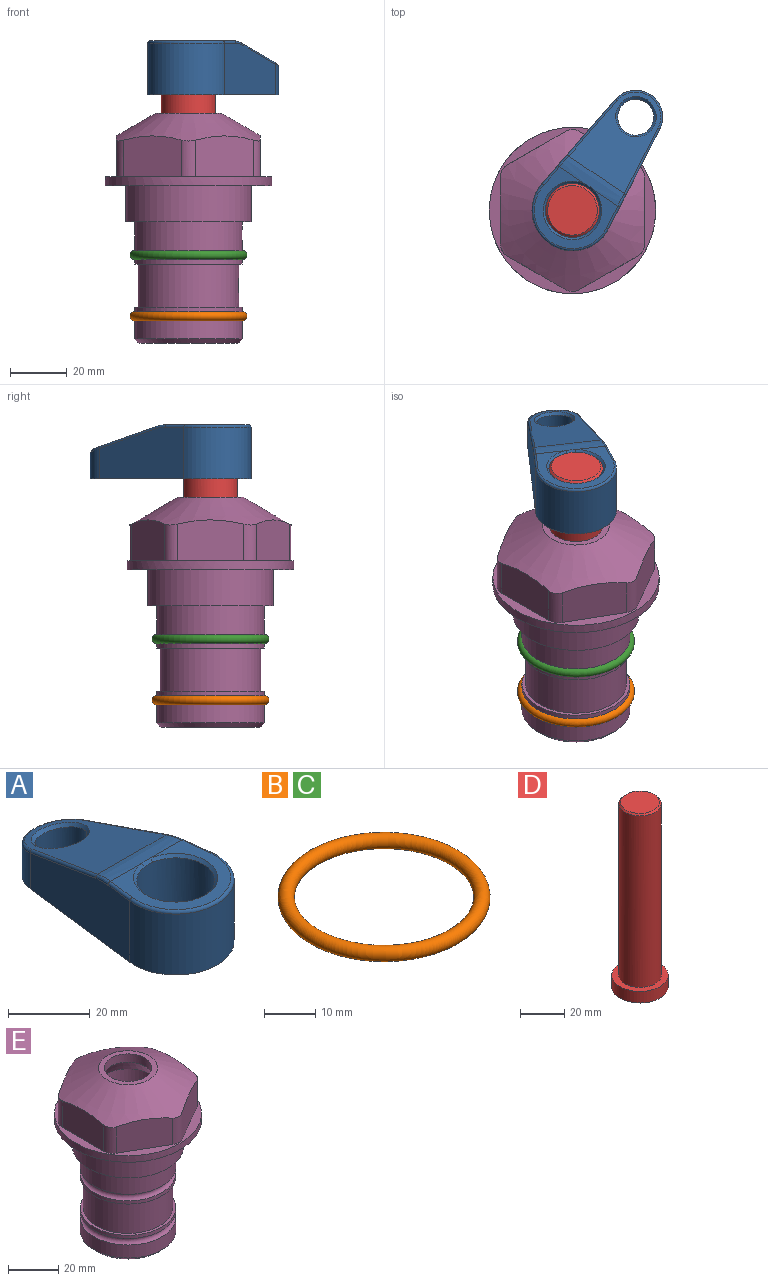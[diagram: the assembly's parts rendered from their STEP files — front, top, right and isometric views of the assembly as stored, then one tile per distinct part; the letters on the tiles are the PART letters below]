
ASSEMBLY  parts=5 mates=4
PART A: 31 faces, bbox 31.7x65.5x19.8 mm
  f0: plane 39.12x18.26mm, normal (0.99,0.12,0), area 612.2mm2, adj f1,f4,f7,f11,f13,f15
  f1: cylinder r=9.53mm len=18.91mm, axis (0,0,-1), area 296.1mm2, adj f0,f2,f7,f17
  f2: plane 39.12x18.26mm, normal (-0.99,0.12,0), area 612.2mm2, adj f1,f4,f7,f12,f14,f16
  f3: cylinder r=6.35mm len=12.7mm, axis (0,0,-1), area 362.4mm2, adj f7,f18
  f4: cylinder r=14.29mm len=28.58mm, axis (0,0,-1), area 882.2mm2, adj f0,f2,f7,f10
  f5: cylinder r=9.53mm len=19.05mm, axis (0,0,-1), area 1092.6mm2, adj f7,f19,f20
  f6: plane 26.99x23.69mm, normal (0,0,1), area 216.2mm2, adj f9,f10,f11,f12,f19
  f7: plane 63.5x28.58mm, normal (0,0,-1), area 661.8mm2, adj f0,f1,f2,f3,f4,f5,f22,f23
  f8: plane 33.52x23.6mm, normal (0,0.26,0.97), area 486mm2, adj f9,f15,f16,f17,f18
  f9: cylinder r=19.05mm len=24.72mm, axis (1,0,0), area 120.4mm2, adj f6,f8,f13,f14,f20
  f10: torus R=13.49mm, axis (0,0,1), area 59mm2, adj f4,f6,f11,f12
  f11: cylinder r=0.79mm len=8.67mm, axis (0.12,-0.99,0), area 10.8mm2, adj f0,f6,f10,f13
  f12: cylinder r=0.79mm len=8.67mm, axis (0.12,0.99,0), area 10.8mm2, adj f2,f6,f10,f14
  f13: bspline ~4.95x1.42mm, area 6.1mm2, adj f0,f9,f11,f15
  f14: bspline ~4.95x1.42mm, area 6.1mm2, adj f2,f9,f12,f16
  f15: cylinder r=0.79mm len=25.95mm, axis (0.12,-0.96,0.26), area 32.9mm2, adj f0,f8,f13,f17
  f16: cylinder r=0.79mm len=25.95mm, axis (0.12,0.96,-0.26), area 32.9mm2, adj f2,f8,f14,f17
  f17: bspline ~18.91x8.38mm, area 30mm2, adj f1,f8,f15,f16
  f18: bspline ~14.29x14.29mm, area 48.3mm2, adj f3,f8
  f19: cone r=9.53mm half-angle=45deg, axis (0,0,1), area 66.5mm2, adj f5,f6,f20
  f20: bspline ~3.22x0.96mm, area 3.5mm2, adj f5,f9,f19
  f21: plane 2.75x2.72mm, normal (0,0,-1), area 2.9mm2, adj f23,f25,f28
  f22: plane 23.05x15.88mm, normal (-0.99,-0.12,0), area 323.6mm2, adj f7,f25,f26,f27,f28,f29
  f23: plane 23.05x15.88mm, normal (0.99,-0.12,0), area 323.6mm2, adj f7,f21,f25,f27,f28,f30
  f24: cylinder r=9.53mm len=10.69mm, axis (0,0,-1), area 114.7mm2, adj f7,f27,f29,f30
  f25: cylinder r=12.7mm len=20.59mm, axis (0,0,-1), area 381.1mm2, adj f7,f21,f22,f23,f26,f28
  f26: plane 2.75x2.72mm, normal (0,0,-1), area 2.9mm2, adj f22,f25,f28
  f27: plane 19.72x18.37mm, normal (0,-0.26,-0.97), area 291.8mm2, adj f22,f23,f24,f28,f29,f30
  f28: cylinder r=15.88mm len=19.92mm, axis (1,0,0), area 54.8mm2, adj f21,f22,f23,f25,f26,f27
  f29: cylinder r=1.59mm len=11mm, axis (0,0,-1), area 34.7mm2, adj f7,f22,f24,f27
  f30: cylinder r=1.59mm len=11mm, axis (0,0,-1), area 34.7mm2, adj f7,f23,f24,f27
PART B: 1 faces, bbox 44.7x44.7x3.2 mm
  f0: torus R=19.05mm, axis (0,0,1), area 1193.9mm2
PART C: same geometry as B
PART D: 6 faces, bbox 25.4x25.4x101.6 mm
  f0: plane 17.46x17.46mm, normal (0,0,1), area 239.5mm2, adj f5
  f1: plane 25.4x25.4mm, normal (0,0,-1), area 506.7mm2, adj f2
  f2: cylinder r=12.7mm len=25.4mm, axis (0,0,1), area 506.7mm2, adj f1,f3
  f3: plane 25.4x25.4mm, normal (0,0,1), area 221.7mm2, adj f2,f4
  f4: cylinder r=9.53mm len=94.46mm, axis (0,0,1), area 5653mm2, adj f3,f5
  f5: cone r=8.73mm half-angle=45deg, axis (0,0,-1), area 64.4mm2, adj f0,f4
PART E: 36 faces, bbox 58.7x58.7x81 mm
  f0: cylinder r=17.78mm len=35.56mm, axis (0,0,1), area 1670.8mm2, adj f23,f24,f31
  f1: cylinder r=19.05mm len=38.1mm, axis (0,0,1), area 1191.9mm2, adj f26,f27,f30
  f2: plane 58.66x58.66mm, normal (0,0,-1), area 1150.6mm2, adj f3,f28
  f3: cylinder r=29.33mm len=58.66mm, axis (0,0,-1), area 585.1mm2, adj f2,f4
  f4: plane 58.66x58.66mm, normal (0,0,1), area 475.9mm2, adj f3,f5,f6,f7,f8,f9,f10,f11
  f5: plane 20.32x14.34mm, normal (-0.5,0.87,0), area 324.4mm2, adj f4,f15,f16,f17
  f6: plane 20.32x14.34mm, normal (0.5,0.87,0), area 324.4mm2, adj f4,f14,f15,f17
  f7: plane 23.48x14.34mm, normal (1,0,0), area 324.4mm2, adj f4,f13,f14,f17
  f8: plane 20.32x14.34mm, normal (0.5,-0.87,0), area 324.4mm2, adj f4,f12,f13,f17
  f9: plane 20.32x14.34mm, normal (-0.5,-0.87,0), area 324.4mm2, adj f4,f11,f12,f17
  f10: plane 23.48x14.34mm, normal (-1,0,0), area 324.4mm2, adj f4,f11,f16,f17
  f11: cylinder r=5.08mm len=12.85mm, axis (0,0,-1), area 67.2mm2, adj f4,f9,f10,f17
  f12: cylinder r=5.08mm len=12.85mm, axis (0,0,-1), area 67.2mm2, adj f4,f8,f9,f17
  f13: cylinder r=5.08mm len=12.85mm, axis (0,0,-1), area 67.2mm2, adj f4,f7,f8,f17
  f14: cylinder r=5.08mm len=12.85mm, axis (0,0,-1), area 67.2mm2, adj f4,f6,f7,f17
  f15: cylinder r=5.08mm len=12.85mm, axis (0,0,-1), area 67.2mm2, adj f4,f5,f6,f17
  f16: cylinder r=5.08mm len=12.85mm, axis (0,0,-1), area 67.2mm2, adj f4,f5,f10,f17
  f17: cone r=11.73mm half-angle=60deg, axis (0,0,-1), area 2071.8mm2, adj f5,f6,f7,f8,f9,f10,f11,f12
  f18: plane 23.46x23.46mm, normal (0,0,1), area 147.4mm2, adj f17,f35
  f19: plane 34.93x34.93mm, normal (0,0,-1), area 958mm2, adj f29
  f20: cylinder r=19.05mm len=38.1mm, axis (0,0,1), area 760.1mm2, adj f21,f29
  f21: torus R=19.05mm, axis (0,0,1), area 565.3mm2, adj f20,f22
  f22: cylinder r=19.05mm len=38.1mm, axis (0,0,1), area 190mm2, adj f21,f23
  f23: plane 38.1x38.1mm, normal (0,0,1), area 146.9mm2, adj f0,f22
  f24: plane 38.1x38.1mm, normal (0,0,-1), area 146.9mm2, adj f0,f25
  f25: cylinder r=19.05mm len=38.1mm, axis (0,0,1), area 190mm2, adj f24,f26
  f26: torus R=19.05mm, axis (0,0,1), area 565.3mm2, adj f1,f25
  f27: plane 44.45x44.45mm, normal (0,0,-1), area 411.7mm2, adj f1,f28
  f28: cylinder r=22.23mm len=44.45mm, axis (0,0,1), area 1773.5mm2, adj f2,f27
  f29: cone r=19.05mm half-angle=45deg, axis (0,0,1), area 257.5mm2, adj f19,f20
  f30: cylinder r=3.17mm len=6.75mm, axis (-1,0,0), area 128mm2, adj f1,f33
  f31: cylinder r=3.17mm len=6.35mm, axis (-1,0,0), area 102.5mm2, adj f0,f33
  f32: plane 25.4x25.4mm, normal (0,0,1), area 506.7mm2, adj f33
  f33: cylinder r=12.7mm len=66.42mm, axis (0,0,-1), area 5236.2mm2, adj f30,f31,f32,f34
  f34: cone r=9.53mm half-angle=30deg, axis (0,0,-1), area 443.4mm2, adj f33,f35
  f35: cylinder r=9.53mm len=19.05mm, axis (0,0,-1), area 240.9mm2, adj f18,f34
PLACE A rot(axis=(0,0,-1),34.1deg) t=(0,0,-12.45)mm
PLACE B t=(0,0,-21.59)mm
PLACE C at identity
PLACE D rot(axis=(0,0,-1),34.1deg) t=(0,0,-12.45)mm
PLACE E at identity fixed
MATE fastened C.f0 <-> E.f0  axis (0,0,1) through (0,0,-24.51)mm
MATE fastened A.f4 <-> D.f2  axis (0,0,-1) through (0,0,50.26)mm
MATE fastened B.f0 <-> E.f0  axis (0,0,1) through (0,0,-46.1)mm
MATE cylindrical D.f2 <-> E.f0  axis (0,0,-1) through (0,0,-50.55)mm
